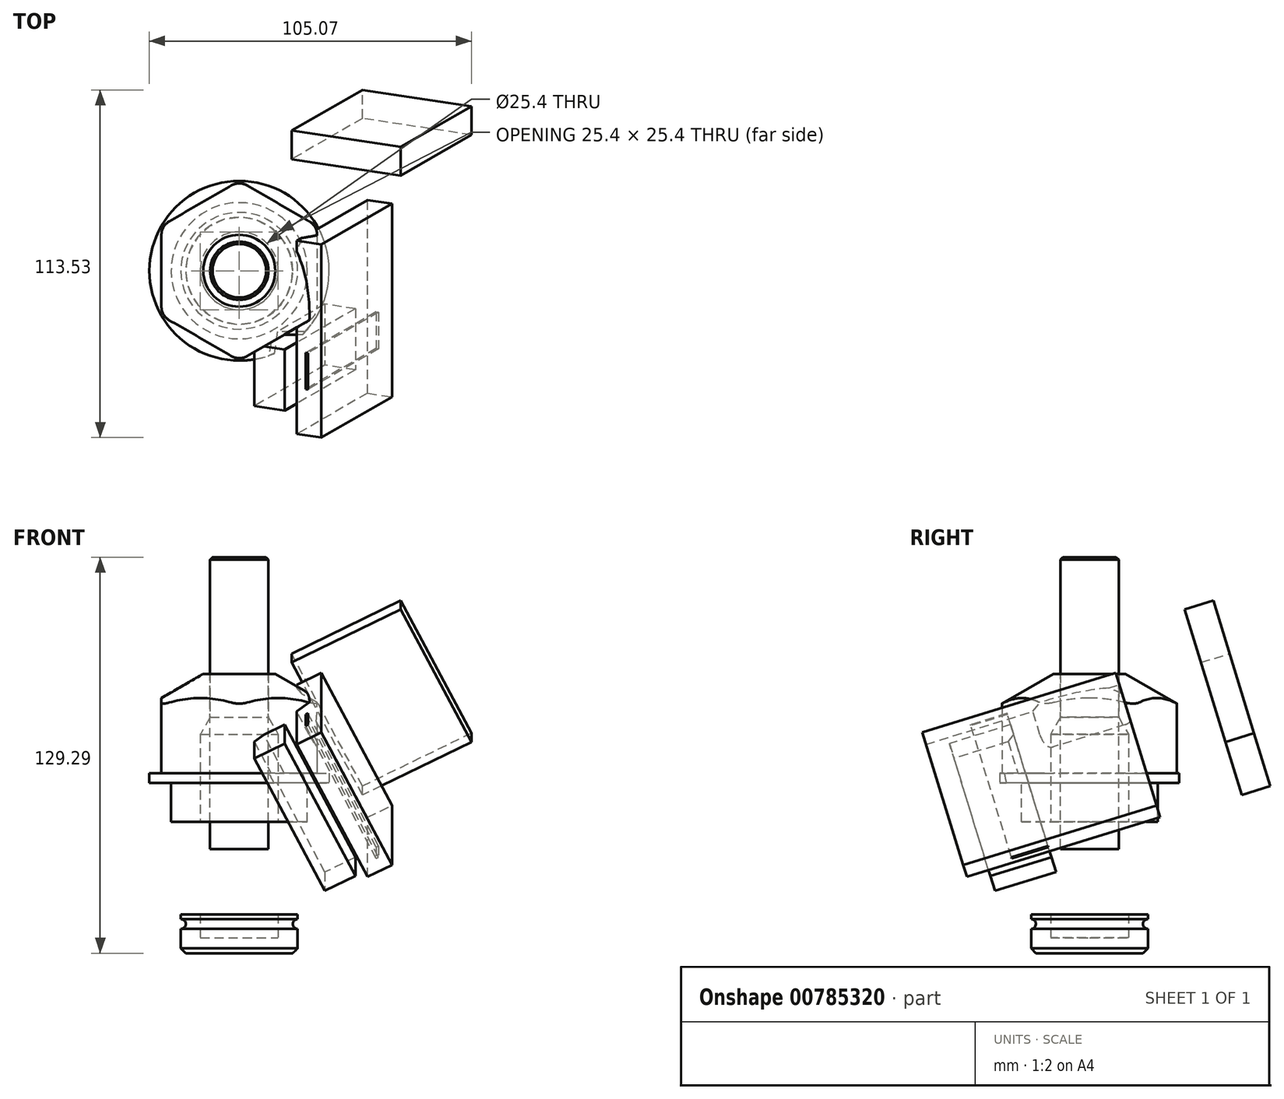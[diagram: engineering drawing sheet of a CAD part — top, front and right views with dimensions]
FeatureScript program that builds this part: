
annotation { "Feature Type Name" : "Feature", "Feature Type Description" : "" }
export const myFeature = defineFeature(function(context is Context, id is Id, definition is map)
    precondition{}
    {
        {
            var Q0;
            Q0=qCreatedBy(makeId("Top.planeOp"),FACE);
            var sketch = newSketch(context, id + "F0", { "sketchPlane" : qUnion([Q0])});
            skCircle(sketch, "E0", {"center": v(0, 0) * mm, "radius": 29.33 * mm});
            skLineSegment(sketch, "E1", {"start": v(0, 29.33) * mm, "end": v(0, -29.33) * mm, "construction": true});
            skLineSegment(sketch, "E2", {"start": v(-25.4, 14.66) * mm, "end": v(25.4, -14.66) * mm, "construction": true});
            skLineSegment(sketch, "E3", {"start": v(-25.4, -14.66) * mm, "end": v(25.4, 14.66) * mm, "construction": true});
            skLineSegment(sketch, "E4", {"start": v(-25.4, 14.66) * mm, "end": v(0, 29.33) * mm});
            skLineSegment(sketch, "E5", {"start": v(0, 29.33) * mm, "end": v(25.4, 14.66) * mm});
            skLineSegment(sketch, "E6", {"start": v(25.4, 14.66) * mm, "end": v(25.4, -14.66) * mm});
            skLineSegment(sketch, "E7", {"start": v(25.4, -14.66) * mm, "end": v(0, -29.33) * mm});
            skLineSegment(sketch, "E8", {"start": v(0, -29.33) * mm, "end": v(-25.4, -14.66) * mm});
            skLineSegment(sketch, "E9", {"start": v(-25.4, -14.66) * mm, "end": v(-25.4, 14.66) * mm});
            skCircle(sketch, "E10", {"center": v(0, 0) * mm, "radius": 7.94 * mm});
            skSolve(sketch);
        }
        {
            var Q0;
            Q0=makeQuery(id+"F0.imprint","IMPRINT",FACE,{"disambiguationData":[TD([[makeQuery(id+"F0.imprint","IMPRINT",EDGE,{"derivedFrom":sQuery(id+"F0.wireOp",EDGE,"E10")}),1.0]])]});
            var Q1;
            Q1=makeQuery(id+"F0.imprint","IMPRINT",FACE,{"disambiguationData":[TD([[makeQuery(id+"F0.imprint","IMPRINT",EDGE,{"derivedFrom":sQuery(id+"F0.wireOp",EDGE,"E4")}),-1.0]])]});
            extrude(context, id + "F1", {"entities" : qUnion([Q0, Q1]), "depth" : 35.56 * mm});
        }
        {
            var Q0;
            {var subQ0=sQuery(id+"F0.wireOp",EDGE,"E8");Q0=makeQuery(id+"F0.imprint","IMPRINT",FACE,{"disambiguationData":[TD([[makeQuery(id+"F0.imprint","IMPRINT",EDGE,{"derivedFrom":subQ0}),1.0]])]});}
            var Q1;
            {var subQ0=sQuery(id+"F0.wireOp",EDGE,"E7");Q1=makeQuery(id+"F0.imprint","IMPRINT",FACE,{"disambiguationData":[TD([[makeQuery(id+"F0.imprint","IMPRINT",EDGE,{"derivedFrom":subQ0}),1.0]])]});}
            var Q2;
            {var subQ0=sQuery(id+"F0.wireOp",EDGE,"E6");Q2=makeQuery(id+"F0.imprint","IMPRINT",FACE,{"disambiguationData":[TD([[makeQuery(id+"F0.imprint","IMPRINT",EDGE,{"derivedFrom":subQ0}),1.0]])]});}
            var Q3;
            Q3=makeQuery(id+"F0.imprint","IMPRINT",FACE,{"disambiguationData":[TD([[makeQuery(id+"F0.imprint","IMPRINT",EDGE,{"derivedFrom":sQuery(id+"F0.wireOp",EDGE,"E4")}),-1.0]])]});
            var Q4;
            {var subQ0=sQuery(id+"F0.wireOp",EDGE,"E5");Q4=makeQuery(id+"F0.imprint","IMPRINT",FACE,{"disambiguationData":[TD([[makeQuery(id+"F0.imprint","IMPRINT",EDGE,{"derivedFrom":subQ0}),1.0]])]});}
            var Q5;
            {var subQ0=sQuery(id+"F0.wireOp",EDGE,"E4");Q5=makeQuery(id+"F0.imprint","IMPRINT",FACE,{"disambiguationData":[TD([[makeQuery(id+"F0.imprint","IMPRINT",EDGE,{"derivedFrom":subQ0}),1.0]])]});}
            var Q6;
            {var subQ0=sQuery(id+"F0.wireOp",EDGE,"E9");Q6=makeQuery(id+"F0.imprint","IMPRINT",FACE,{"disambiguationData":[TD([[makeQuery(id+"F0.imprint","IMPRINT",EDGE,{"derivedFrom":subQ0}),1.0]])]});}
            extrude(context, id + "F2", {"entities" : qUnion([Q0, Q1, Q2, Q3, Q4, Q5, Q6]), "operationType" : NewBodyOperationType.ADD, "depth" : 3.17 * mm});
        }
        {
            var Q0;
            Q0=makeQuery(id+"F1.opExtrude","SWEPT_EDGE",EDGE,{"disambiguationData":[OSD([sQuery(id+"F0.wireOp",EDGE,"E0"),sQuery(id+"F0.wireOp",EDGE,"E7"),sQuery(id+"F0.wireOp",EDGE,"E8")])]});
            var Q1;
            Q1=makeQuery(id+"F1.opExtrude","SWEPT_EDGE",EDGE,{"disambiguationData":[OSD([sQuery(id+"F0.wireOp",EDGE,"E0"),sQuery(id+"F0.wireOp",EDGE,"E6"),sQuery(id+"F0.wireOp",EDGE,"E7")])]});
            var Q2;
            Q2=makeQuery(id+"F1.opExtrude","SWEPT_EDGE",EDGE,{"disambiguationData":[OSD([sQuery(id+"F0.wireOp",EDGE,"E0"),sQuery(id+"F0.wireOp",EDGE,"E5"),sQuery(id+"F0.wireOp",EDGE,"E6")])]});
            var Q3;
            Q3=makeQuery(id+"F1.opExtrude","SWEPT_EDGE",EDGE,{"disambiguationData":[OSD([sQuery(id+"F0.wireOp",EDGE,"E0"),sQuery(id+"F0.wireOp",EDGE,"E4"),sQuery(id+"F0.wireOp",EDGE,"E5")])]});
            var Q4;
            Q4=makeQuery(id+"F1.opExtrude","SWEPT_EDGE",EDGE,{"disambiguationData":[OSD([sQuery(id+"F0.wireOp",EDGE,"E0"),sQuery(id+"F0.wireOp",EDGE,"E4"),sQuery(id+"F0.wireOp",EDGE,"E9")])]});
            var Q5;
            Q5=makeQuery(id+"F1.opExtrude","SWEPT_EDGE",EDGE,{"disambiguationData":[OSD([sQuery(id+"F0.wireOp",EDGE,"E0"),sQuery(id+"F0.wireOp",EDGE,"E8"),sQuery(id+"F0.wireOp",EDGE,"E9")])]});
            fillet(context, id + "F3", {"entities" : qUnion([Q0, Q1, Q2, Q3, Q4, Q5]), "radius" : 5.08 * mm, "tangentPropagation" : true, "allowEdgeOverflow" : false});
        }
        {
            var Q0;
            Q0=qCreatedBy(makeId("Right.planeOp"),FACE);
            var sketch = newSketch(context, id + "F4", { "sketchPlane" : qUnion([Q0])});
            skLineSegment(sketch, "E11", {"start": v(0, 52) * mm, "end": v(0, 0) * mm, "construction": true});
            skLineSegment(sketch, "E12", {"start": v(11.73, 35.56) * mm, "end": v(35.4, 21.9) * mm});
            skLineSegment(sketch, "E13", {"start": v(35.4, 21.9) * mm, "end": v(35.4, 35.56) * mm});
            skLineSegment(sketch, "E14", {"start": v(35.4, 35.56) * mm, "end": v(11.73, 35.56) * mm});
            skLineSegment(sketch, "E15.0", {"start": v(11.73, 35.56) * mm, "end": v(-11.73, 35.56) * mm});
            skLineSegment(sketch, "E16.bottom", {"start": v(0, 0) * mm, "end": v(22.23, 0) * mm});
            skLineSegment(sketch, "E16.top", {"start": v(0, -12.7) * mm, "end": v(22.23, -12.7) * mm});
            skLineSegment(sketch, "E16.left", {"start": v(0, 0) * mm, "end": v(0, -12.7) * mm});
            skLineSegment(sketch, "E16.right", {"start": v(22.23, 0) * mm, "end": v(22.23, -12.7) * mm});
            skLineSegment(sketch, "E17.bottom", {"start": v(0, -12.7) * mm, "end": v(19.05, -12.7) * mm});
            skLineSegment(sketch, "E17.top", {"start": v(0, -27.69) * mm, "end": v(19.05, -27.69) * mm});
            skLineSegment(sketch, "E17.left", {"start": v(0, -12.7) * mm, "end": v(0, -27.69) * mm});
            skLineSegment(sketch, "E17.right", {"start": v(19.05, -12.7) * mm, "end": v(19.05, -27.69) * mm});
            skLineSegment(sketch, "E18.bottom", {"start": v(17.78, -27.69) * mm, "end": v(0, -27.69) * mm});
            skLineSegment(sketch, "E18.top", {"start": v(17.78, -42.93) * mm, "end": v(0, -42.93) * mm});
            skLineSegment(sketch, "E18.left", {"start": v(17.78, -27.69) * mm, "end": v(17.78, -42.93) * mm});
            skLineSegment(sketch, "E18.right", {"start": v(0, -27.69) * mm, "end": v(0, -42.93) * mm});
            skLineSegment(sketch, "E19.bottom", {"start": v(0, -42.93) * mm, "end": v(19.05, -42.93) * mm});
            skLineSegment(sketch, "E19.top", {"start": v(0, -55.63) * mm, "end": v(19.05, -55.63) * mm});
            skLineSegment(sketch, "E19.left", {"start": v(0, -42.93) * mm, "end": v(0, -55.63) * mm});
            skLineSegment(sketch, "E19.right", {"start": v(19.05, -42.93) * mm, "end": v(19.05, -55.63) * mm});
            skCircle(sketch, "E20", {"center": v(19.05, -24.51) * mm, "radius": 1.59 * mm});
            skCircle(sketch, "E21", {"center": v(19.05, -46.1) * mm, "radius": 1.59 * mm});
            skCircle(sketch, "E22", {"center": v(0, -17.46) * mm, "radius": 3.18 * mm});
            skCircle(sketch, "E23", {"center": v(0, -35.3) * mm, "radius": 3.18 * mm});
            skSolve(sketch);
        }
        {
            var Q0;
            Q0=makeQuery(id+"F4.imprint","IMPRINT",FACE,{"disambiguationData":[TD([[makeQuery(id+"F4.imprint","IMPRINT",EDGE,{"derivedFrom":sQuery(id+"F4.wireOp",EDGE,"E12")}),1.0]])]});
            var Q1;
            Q1=sQuery(id+"F4.wireOp",EDGE,"E11");
            revolve(context, id + "F5", {"operationType" : NewBodyOperationType.REMOVE, "entities" : qUnion([Q0]), "axis" : qUnion([Q1]), "revolveType" : RevolveType.FULL, "oppositeDirection" : true});
        }
        {
            var Q0;
            {var subQ7=sQuery(id+"F4.wireOp",EDGE,"E18.bottom");Q0=makeQuery(id+"F4.imprint","IMPRINT",FACE,{"disambiguationData":[TD([[makeQuery(id+"F4.imprint","IMPRINT",EDGE,{"derivedFrom":subQ7}),1.0]])]});}
            var Q1;
            {var subQ10=sQuery(id+"F4.wireOp",EDGE,"E17.bottom");Q1=makeQuery(id+"F4.imprint","IMPRINT",FACE,{"disambiguationData":[TD([[makeQuery(id+"F4.imprint","IMPRINT",EDGE,{"derivedFrom":subQ10}),-1.0]])]});}
            var Q2;
            Q2=makeQuery(id+"F4.imprint","IMPRINT",FACE,{"disambiguationData":[TD([[makeQuery(id+"F4.imprint","IMPRINT",EDGE,{"derivedFrom":sQuery(id+"F4.wireOp",EDGE,"E16.bottom")}),-1.0]])]});
            var Q3;
            {var subQ4=sQuery(id+"F4.wireOp",EDGE,"E19.top");Q3=makeQuery(id+"F4.imprint","IMPRINT",FACE,{"disambiguationData":[TD([[makeQuery(id+"F4.imprint","IMPRINT",EDGE,{"derivedFrom":subQ4}),1.0]])]});}
            var Q4;
            Q4=sQuery(id+"F4.wireOp",EDGE,"E11");
            revolve(context, id + "F6", {"operationType" : NewBodyOperationType.ADD, "entities" : qUnion([Q0, Q1, Q2, Q3]), "axis" : qUnion([Q4]), "revolveType" : RevolveType.FULL});
        }
        {
            var Q0;
            Q0=makeQuery(id+"F6.opRevolve","SWEPT_EDGE",EDGE,{"disambiguationData":[OSD([sQuery(id+"F4.wireOp",EDGE,"E19.top"),sQuery(id+"F4.wireOp",EDGE,"E19.right")])]});
            chamfer(context, id + "F7", {"entities" : qUnion([Q0]), "width" : 1.59 * mm, "tangentPropagation" : true});
        }
        {
            var Q0;
            {var subQ0=sQuery(id+"F4.wireOp",EDGE,"E16.right");var subQ1=sQuery(id+"F4.wireOp",EDGE,"E20");var subQ3=makeQuery(id+"F4.imprint","INTERSECT",VERTEX,{"disambiguationData":[OD(0.0)],"derivedFrom":[subQ0,subQ1]});Q0=makeQuery(id+"F4.imprint","IMPRINT",FACE,{"disambiguationData":[TD([[makeQuery(id+"F4.imprint","SKETCH_ENTITY",EDGE,{"disambiguationData":[TD([[subQ3,-1.0]])],"sketchEntityId":"E16.right"}),1.0]])]});}
            var Q1;
            {var subQ0=sQuery(id+"F4.wireOp",EDGE,"E20");var subQ1=sQuery(id+"F4.wireOp",EDGE,"E17.right");var subQ3=makeQuery(id+"F4.imprint","INTERSECT",VERTEX,{"disambiguationData":[OD(0.0)],"derivedFrom":[subQ1,subQ0]});Q1=makeQuery(id+"F4.imprint","IMPRINT",FACE,{"disambiguationData":[TD([[makeQuery(id+"F4.imprint","IMPRINT",EDGE,{"disambiguationData":[TD([[subQ3,-1.0]])],"derivedFrom":subQ1}),-1.0]])]});}
            var Q2;
            {var subQ0=sQuery(id+"F4.wireOp",EDGE,"E20");var subQ1=sQuery(id+"F4.wireOp",EDGE,"E17.right");var subQ3=makeQuery(id+"F4.imprint","INTERSECT",VERTEX,{"disambiguationData":[OD(0.0)],"derivedFrom":[subQ1,subQ0]});Q2=makeQuery(id+"F4.imprint","IMPRINT",FACE,{"disambiguationData":[TD([[makeQuery(id+"F4.imprint","IMPRINT",EDGE,{"disambiguationData":[TD([[subQ3,-1.0]])],"derivedFrom":subQ1}),1.0]])]});}
            var Q3;
            Q3=sQuery(id+"F4.wireOp",EDGE,"E11");
            revolve(context, id + "F8", {"entities" : qUnion([Q0, Q1, Q2]), "axis" : qUnion([Q3]), "revolveType" : RevolveType.FULL});
        }
        {
            var Q0;
            {var subQ0=sQuery(id+"F4.wireOp",EDGE,"E22");var subQ1=sQuery(id+"F4.wireOp",EDGE,"E17.left");var subQ3=makeQuery(id+"F4.imprint","INTERSECT",VERTEX,{"disambiguationData":[OD(0.0)],"derivedFrom":[subQ1,subQ0]});Q0=makeQuery(id+"F4.imprint","IMPRINT",FACE,{"disambiguationData":[TD([[makeQuery(id+"F4.imprint","IMPRINT",EDGE,{"disambiguationData":[TD([[subQ3,-1.0]])],"derivedFrom":subQ1}),-1.0]])]});}
            var Q1;
            {var subQ0=sQuery(id+"F4.wireOp",EDGE,"E22");var subQ1=sQuery(id+"F4.wireOp",EDGE,"E17.left");var subQ3=makeQuery(id+"F4.imprint","INTERSECT",VERTEX,{"disambiguationData":[OD(0.0)],"derivedFrom":[subQ1,subQ0]});Q1=makeQuery(id+"F4.imprint","IMPRINT",FACE,{"disambiguationData":[TD([[makeQuery(id+"F4.imprint","IMPRINT",EDGE,{"disambiguationData":[TD([[subQ3,-1.0]])],"derivedFrom":subQ1}),1.0]])]});}
            var Q2;
            {var subQ0=sQuery(id+"F4.wireOp",EDGE,"E23");var subQ1=sQuery(id+"F4.wireOp",EDGE,"E18.right");var subQ3=makeQuery(id+"F4.imprint","INTERSECT",VERTEX,{"disambiguationData":[OD(0.0)],"derivedFrom":[subQ1,subQ0]});Q2=makeQuery(id+"F4.imprint","IMPRINT",FACE,{"disambiguationData":[TD([[makeQuery(id+"F4.imprint","IMPRINT",EDGE,{"disambiguationData":[TD([[subQ3,-1.0]])],"derivedFrom":subQ1}),-1.0]])]});}
            var Q3;
            {var subQ0=sQuery(id+"F4.wireOp",EDGE,"E23");var subQ1=sQuery(id+"F4.wireOp",EDGE,"E18.right");var subQ3=makeQuery(id+"F4.imprint","INTERSECT",VERTEX,{"disambiguationData":[OD(0.0)],"derivedFrom":[subQ1,subQ0]});Q3=makeQuery(id+"F4.imprint","IMPRINT",FACE,{"disambiguationData":[TD([[makeQuery(id+"F4.imprint","IMPRINT",EDGE,{"disambiguationData":[TD([[subQ3,-1.0]])],"derivedFrom":subQ1}),1.0]])]});}
            extrude(context, id + "F9", {"entities" : qUnion([Q0, Q1, Q2, Q3]), "operationType" : NewBodyOperationType.REMOVE, "endBound" : BoundingType.THROUGH_ALL, "depth" : 25.4 * mm});
        }
        {
            var Q0;
            Q0=qCreatedBy(makeId("Right.planeOp"),FACE);
            var sketch = newSketch(context, id + "F10", { "sketchPlane" : qUnion([Q0])});
            skLineSegment(sketch, "E24", {"start": v(0, 73.66) * mm, "end": v(0, -50.55) * mm});
            skLineSegment(sketch, "E25", {"start": v(0, -50.55) * mm, "end": v(12.7, -50.55) * mm});
            skLineSegment(sketch, "E26", {"start": v(12.7, -50.55) * mm, "end": v(12.7, 15.88) * mm});
            skLineSegment(sketch, "E27", {"start": v(12.7, 15.88) * mm, "end": v(0, 15.88) * mm});
            skLineSegment(sketch, "E28", {"start": v(9.53, -21.6) * mm, "end": v(9.53, 73.66) * mm});
            skLineSegment(sketch, "E29", {"start": v(9.52, 73.66) * mm, "end": v(0, 73.66) * mm});
            skLineSegment(sketch, "E30", {"start": v(9.53, 21.37) * mm, "end": v(12.7, 15.88) * mm});
            skLineSegment(sketch, "E31.rect.bottom", {"start": v(12.7, -27.94) * mm, "end": v(-12.7, -27.94) * mm});
            skLineSegment(sketch, "E31.rect.top", {"start": v(12.7, -21.59) * mm, "end": v(-12.7, -21.59) * mm});
            skLineSegment(sketch, "E31.rect.left", {"start": v(12.7, -27.94) * mm, "end": v(12.7, -21.59) * mm});
            skLineSegment(sketch, "E31.rect.right", {"start": v(-12.7, -27.94) * mm, "end": v(-12.7, -21.59) * mm});
            skPoint(sketch, "E31.rect.middle", {"position": v(0, -24.77) * mm});
            skSolve(sketch);
        }
        {
            var Q0;
            {var subQ0=sQuery(id+"F10.wireOp",EDGE,"E29");Q0=makeQuery(id+"F10.imprint","IMPRINT",FACE,{"disambiguationData":[TD([[makeQuery(id+"F10.imprint","IMPRINT",EDGE,{"derivedFrom":subQ0}),1.0]])]});}
            var Q1;
            {var subQ0=sQuery(id+"F10.wireOp",EDGE,"E30");Q1=makeQuery(id+"F10.imprint","IMPRINT",FACE,{"disambiguationData":[TD([[makeQuery(id+"F10.imprint","IMPRINT",EDGE,{"derivedFrom":subQ0}),-1.0]])]});}
            var Q2;
            {var subQ1=sQuery(id+"F10.wireOp",EDGE,"E24");var subQ5=sQuery(id+"F10.wireOp",EDGE,"E27");var subQ7=makeQuery(id+"F10.imprint","INTERSECT",VERTEX,{"derivedFrom":[subQ1,subQ5]});Q2=makeQuery(id+"F10.imprint","IMPRINT",FACE,{"disambiguationData":[TD([[makeQuery(id+"F10.imprint","IMPRINT",EDGE,{"disambiguationData":[TD([[subQ7,-1.0]])],"derivedFrom":subQ1}),1.0]])]});}
            var Q3;
            {var subQ0=sQuery(id+"F10.wireOp",EDGE,"E31.rect.top");var subQ3=sQuery(id+"F10.wireOp",EDGE,"E28");var subQ4=makeQuery(id+"F10.imprint","INTERSECT",VERTEX,{"derivedFrom":[subQ3,subQ0]});Q3=makeQuery(id+"F10.imprint","IMPRINT",FACE,{"disambiguationData":[TD([[makeQuery(id+"F10.imprint","IMPRINT",EDGE,{"disambiguationData":[TD([[subQ4,-1.0]])],"derivedFrom":subQ3}),-1.0]])]});}
            var Q4;
            {var subQ5=sQuery(id+"F10.wireOp",EDGE,"E25");Q4=makeQuery(id+"F10.imprint","IMPRINT",FACE,{"disambiguationData":[TD([[makeQuery(id+"F10.imprint","IMPRINT",EDGE,{"derivedFrom":subQ5}),1.0]])]});}
            var Q5;
            {var subQ0=sQuery(id+"F10.wireOp",EDGE,"E31.rect.left");Q5=makeQuery(id+"F10.imprint","IMPRINT",FACE,{"disambiguationData":[TD([[makeQuery(id+"F10.imprint","IMPRINT",EDGE,{"derivedFrom":subQ0}),1.0]])]});}
            var Q6;
            Q6=sQuery(id+"F10.wireOp",EDGE,"E24");
            revolve(context, id + "F11", {"operationType" : NewBodyOperationType.REMOVE, "entities" : qUnion([Q0, Q1, Q2, Q3, Q4, Q5]), "axis" : qUnion([Q6]), "revolveType" : RevolveType.FULL, "oppositeDirection" : true});
        }
        {
            var Q0;
            {var subQ0=sQuery(id+"F10.wireOp",EDGE,"E29");Q0=makeQuery(id+"F10.imprint","IMPRINT",FACE,{"disambiguationData":[TD([[makeQuery(id+"F10.imprint","IMPRINT",EDGE,{"derivedFrom":subQ0}),1.0]])]});}
            var Q1;
            {var subQ1=sQuery(id+"F10.wireOp",EDGE,"E24");var subQ5=sQuery(id+"F10.wireOp",EDGE,"E27");var subQ7=makeQuery(id+"F10.imprint","INTERSECT",VERTEX,{"derivedFrom":[subQ1,subQ5]});Q1=makeQuery(id+"F10.imprint","IMPRINT",FACE,{"disambiguationData":[TD([[makeQuery(id+"F10.imprint","IMPRINT",EDGE,{"disambiguationData":[TD([[subQ7,-1.0]])],"derivedFrom":subQ1}),1.0]])]});}
            var Q2;
            {var subQ0=sQuery(id+"F10.wireOp",EDGE,"E31.rect.left");Q2=makeQuery(id+"F10.imprint","IMPRINT",FACE,{"disambiguationData":[TD([[makeQuery(id+"F10.imprint","IMPRINT",EDGE,{"derivedFrom":subQ0}),1.0]])]});}
            var Q3;
            Q3=sQuery(id+"F10.wireOp",EDGE,"E24");
            revolve(context, id + "F12", {"entities" : qUnion([Q0, Q1, Q2]), "axis" : qUnion([Q3]), "revolveType" : RevolveType.FULL});
        }
        {
            var Q0;
            Q0=makeQuery(id+"F12.opRevolve","SWEPT_EDGE",EDGE,{"disambiguationData":[OSD([sQuery(id+"F10.wireOp",EDGE,"E28"),sQuery(id+"F10.wireOp",EDGE,"E29")])]});
            chamfer(context, id + "F13", {"entities" : qUnion([Q0]), "width" : 0.8 * mm, "tangentPropagation" : true});
        }
        {
            var Q0;
            Q0=makeQuery(id+"F1.opExtrude","SWEPT_FACE",FACE,{"disambiguationData":[OSD([sQuery(id+"F0.wireOp",EDGE,"E7")])]});
            var sketch = newSketch(context, id + "F14", { "sketchPlane" : qUnion([Q0])});
            skLineSegment(sketch, "E32", {"start": v(0, 18.96) * mm, "end": v(11.73, 26.18) * mm});
            skSolve(sketch);
        }
        {
            var Q0;
            Q0 = qSketchRegion(id + "F14", true);
            var Q1;
            Q1=sQuery(id+"F14.wireOp",EDGE,"E32");
            extrude(context, id + "F15", {"entities" : qUnion([Q0]), "bodyType" : ToolBodyType.SURFACE, "surfaceEntities" : qUnion([Q1]), "depth" : 25.4 * mm, "offsetDistance" : 25.4 * mm});
        }
        {
            var Q0;
            Q0=makeQuery(id+"F15.opExtrude","SWEPT_FACE",FACE,{"disambiguationData":[OSD([sQuery(id+"F14.wireOp",EDGE,"E32")])]});
            var sketch = newSketch(context, id + "F16", { "sketchPlane" : qUnion([Q0])});
            skLineSegment(sketch, "E33.bottom", {"start": v(32.52, 19) * mm, "end": v(33.33, 19) * mm});
            skLineSegment(sketch, "E33.top", {"start": v(32.52, 31.47) * mm, "end": v(33.33, 31.47) * mm});
            skLineSegment(sketch, "E33.left", {"start": v(32.52, 19) * mm, "end": v(32.52, 31.47) * mm});
            skLineSegment(sketch, "E33.right", {"start": v(33.33, 19) * mm, "end": v(33.33, 31.47) * mm});
            skLineSegment(sketch, "E34.bottom", {"start": v(24.88, 19) * mm, "end": v(13.7, 19) * mm});
            skLineSegment(sketch, "E34.top", {"start": v(24.88, 39.84) * mm, "end": v(13.7, 39.84) * mm});
            skLineSegment(sketch, "E34.left", {"start": v(24.88, 19) * mm, "end": v(24.88, 39.84) * mm});
            skLineSegment(sketch, "E34.right", {"start": v(13.7, 19) * mm, "end": v(13.7, 39.84) * mm});
            skLineSegment(sketch, "E35.bottom", {"start": v(29.3, 47.23) * mm, "end": v(38.25, 47.23) * mm});
            skLineSegment(sketch, "E35.top", {"start": v(29.3, -18.76) * mm, "end": v(38.25, -18.76) * mm});
            skLineSegment(sketch, "E35.left", {"start": v(29.3, 47.23) * mm, "end": v(29.3, -18.76) * mm});
            skLineSegment(sketch, "E35.right", {"start": v(38.25, 47.23) * mm, "end": v(38.25, -18.76) * mm});
            skLineSegment(sketch, "E36.bottom", {"start": v(67.35, -46.34) * mm, "end": v(27.42, -46.34) * mm});
            skLineSegment(sketch, "E36.top", {"start": v(67.35, -56.1) * mm, "end": v(27.42, -56.1) * mm});
            skLineSegment(sketch, "E36.left", {"start": v(67.35, -46.34) * mm, "end": v(67.35, -56.1) * mm});
            skLineSegment(sketch, "E36.right", {"start": v(27.42, -46.34) * mm, "end": v(27.42, -56.1) * mm});
            skSolve(sketch);
        }
        {
            var Q0;
            Q0 = qSketchRegion(id + "F16", true);
            extrude(context, id + "F17", {"entities" : qUnion([Q0]), "operationType" : NewBodyOperationType.ADD, "depth" : 50.8 * mm, "offsetDistance" : 25.4 * mm});
        }
    });
